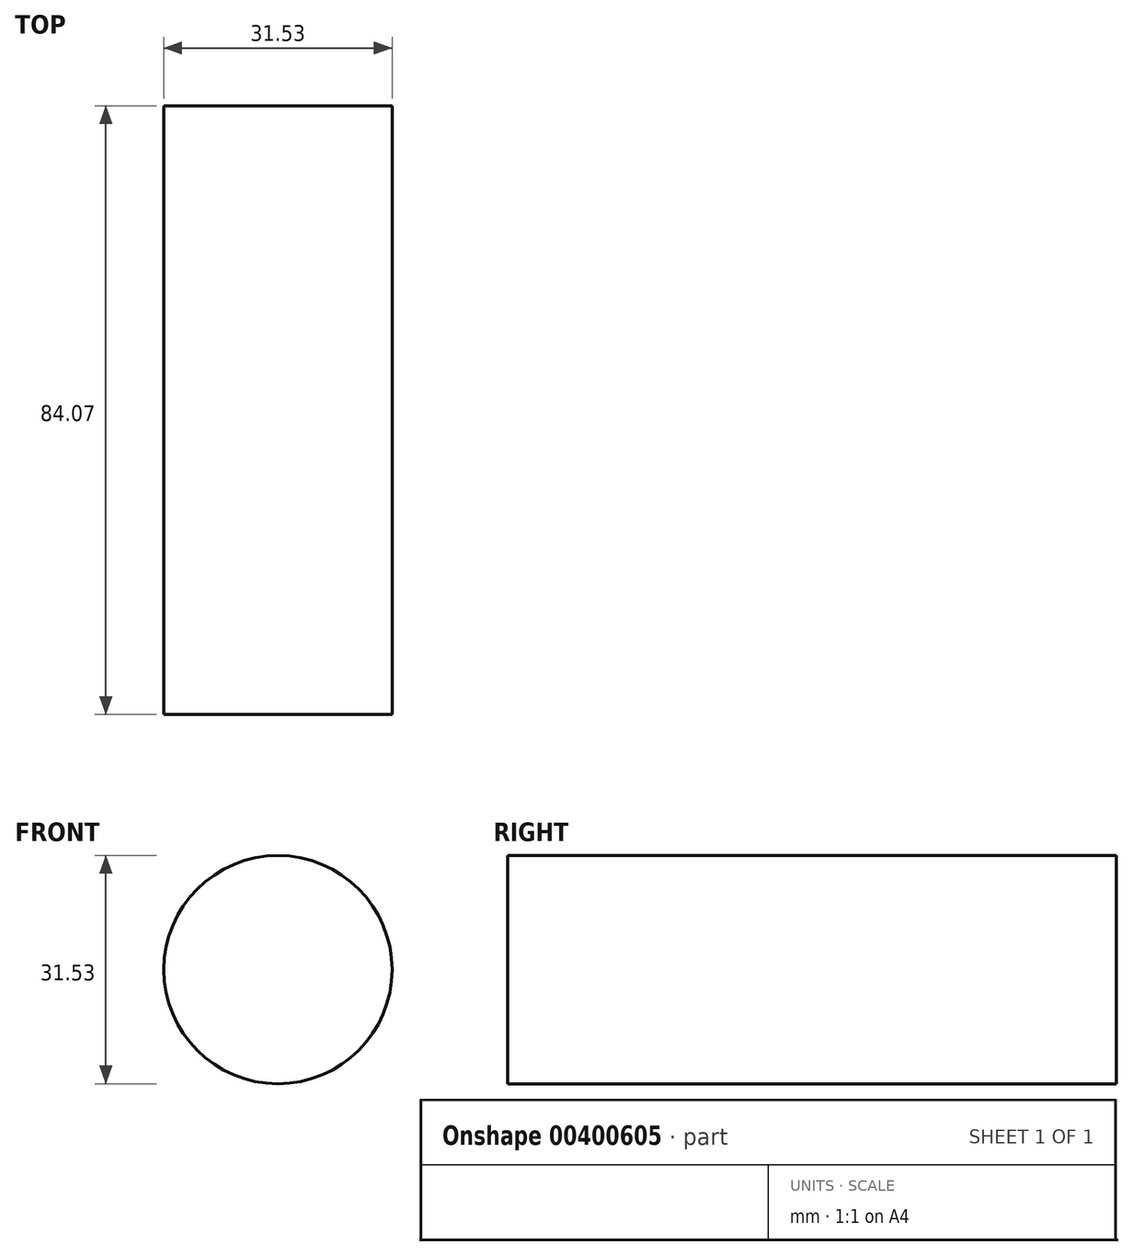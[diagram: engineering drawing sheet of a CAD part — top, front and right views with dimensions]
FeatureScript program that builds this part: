
annotation { "Feature Type Name" : "Feature", "Feature Type Description" : "" }
export const myFeature = defineFeature(function(context is Context, id is Id, definition is map)
    precondition{}
    {
        {
            var Q0;
            Q0=qCreatedBy(makeId("Front.planeOp"),FACE);
            var sketch = newSketch(context, id + "F0", { "sketchPlane" : qUnion([Q0])});
            skCircle(sketch, "E0", {"center": v(22.2, 53.3) * mm, "radius": 15.76 * mm});
            skSolve(sketch);
        }
        {
            var Q0;
            Q0 = qSketchRegion(id + "F0", true);
            extrude(context, id + "F1", {"entities" : qUnion([Q0]), "depth" : 84.07 * mm});
        }
    });
